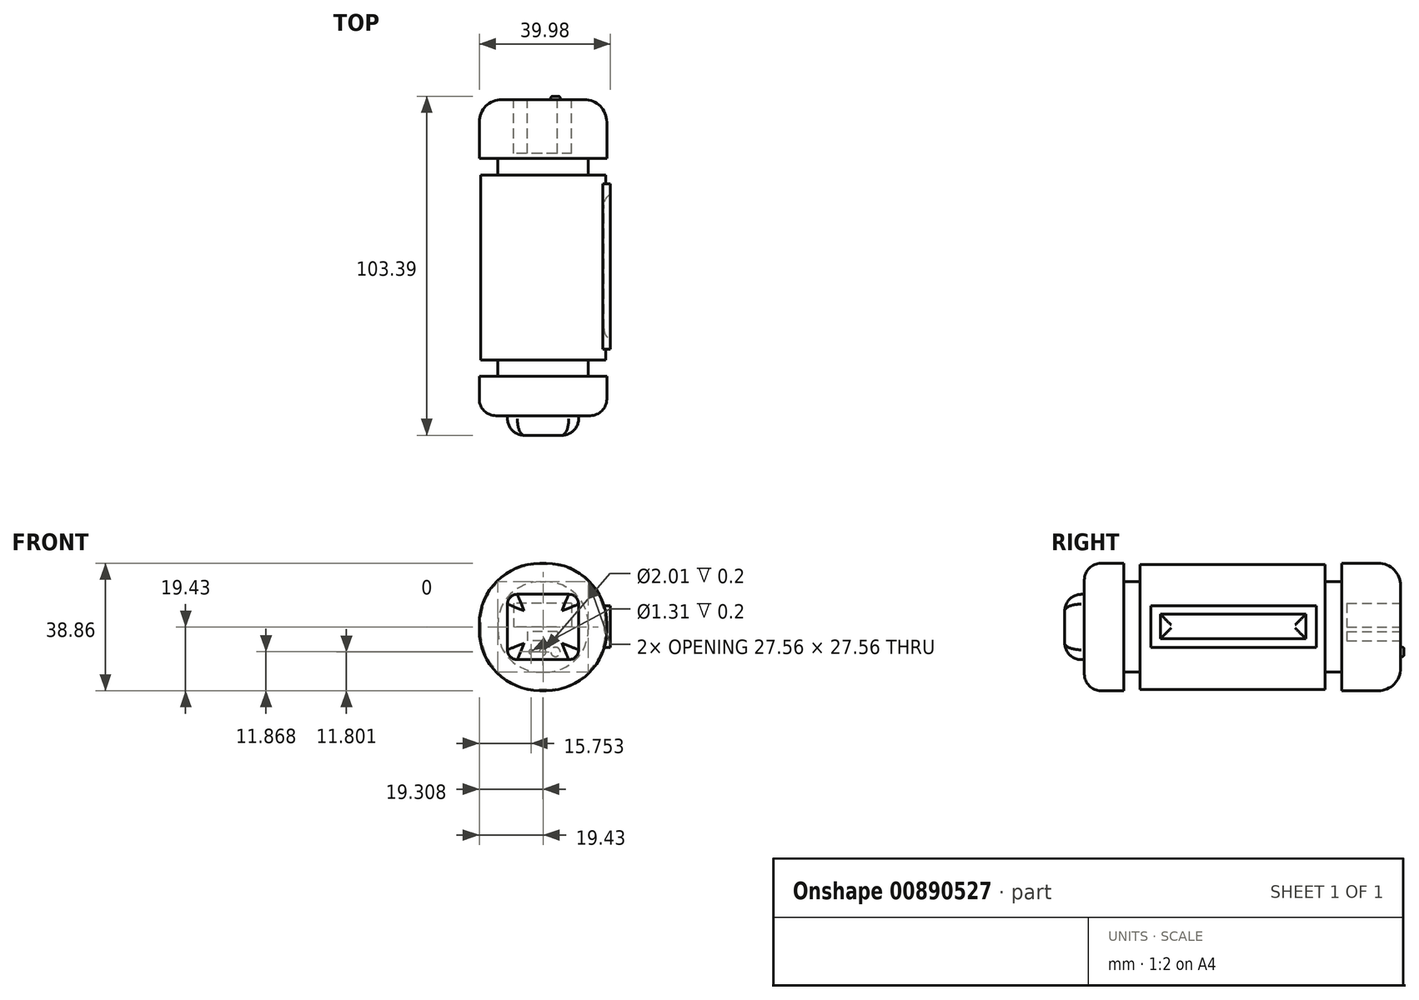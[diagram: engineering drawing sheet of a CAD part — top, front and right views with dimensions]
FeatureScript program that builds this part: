
annotation { "Feature Type Name" : "Feature", "Feature Type Description" : "" }
export const myFeature = defineFeature(function(context is Context, id is Id, definition is map)
    precondition{}
    {
        {
            var Q0;
            Q0=qCreatedBy(makeId("Front.planeOp"),FACE);
            var sketch = newSketch(context, id + "F0", { "sketchPlane" : qUnion([Q0])});
            skLineSegment(sketch, "E0.bottom", {"start": v(19.05, 19.05) * mm, "end": v(-19.05, 19.05) * mm});
            skLineSegment(sketch, "E0.top", {"start": v(19.05, -19.05) * mm, "end": v(-19.05, -19.05) * mm});
            skLineSegment(sketch, "E0.left", {"start": v(19.05, 19.05) * mm, "end": v(19.05, -19.05) * mm});
            skLineSegment(sketch, "E0.right", {"start": v(-19.05, 19.05) * mm, "end": v(-19.05, -19.05) * mm});
            skPoint(sketch, "E0.middle", {"position": v(0, 0) * mm});
            skSolve(sketch);
        }
        {
            var Q0;
            Q0=makeQuery(id+"F0.imprint","IMPRINT",FACE,{"disambiguationData":[TD([[makeQuery(id+"F0.imprint","IMPRINT",EDGE,{"derivedFrom":sQuery(id+"F0.wireOp",EDGE,"E0.bottom")}),1.0]])]});
            extrude(context, id + "F1", {"entities" : qUnion([Q0]), "depth" : 25.4 * mm, "offsetDistance" : 25.4 * mm});
        }
        {
            var Q0;
            Q0=makeQuery(id+"F1.opExtrude","CAP_FACE",FACE,{"disambiguationData":[OSD([sQuery(id+"F0.wireOp",EDGE,"E0.bottom"),sQuery(id+"F0.wireOp",EDGE,"E0.top"),sQuery(id+"F0.wireOp",EDGE,"E0.left"),sQuery(id+"F0.wireOp",EDGE,"E0.right")])],"isStart":false});
            extrude(context, id + "F2", {"entities" : qUnion([Q0]), "operationType" : NewBodyOperationType.ADD, "depth" : 30.99 * mm, "offsetDistance" : 25.4 * mm});
        }
        {
            var Q0;
            {var subQ0=sQuery(id+"F0.wireOp",EDGE,"E0.left");Q0=makeQuery(id+"F2.boolean.opBoolean","MERGE",FACE,{"derivedFrom":[makeQuery(id+"F1.opExtrude","SWEPT_FACE",FACE,{"disambiguationData":[OSD([subQ0])]}),makeQuery(id+"F2.opExtrude","SWEPT_FACE",FACE,{"disambiguationData":[OSD([subQ0])]})]});}
            var sketch = newSketch(context, id + "F3", { "sketchPlane" : qUnion([Q0])});
            skLineSegment(sketch, "E1.bottom", {"start": v(-53.1, 6.48) * mm, "end": v(-2.73, 6.48) * mm});
            skLineSegment(sketch, "E1.top", {"start": v(-53.1, -6.19) * mm, "end": v(-2.73, -6.19) * mm});
            skLineSegment(sketch, "E1.left", {"start": v(-53.1, 6.48) * mm, "end": v(-53.1, -6.19) * mm});
            skLineSegment(sketch, "E1.right", {"start": v(-2.73, 6.48) * mm, "end": v(-2.73, -6.19) * mm});
            skSolve(sketch);
        }
        {
            var Q0;
            Q0=makeQuery(id+"F3.imprint","IMPRINT",FACE,{"disambiguationData":[TD([[makeQuery(id+"F3.imprint","IMPRINT",EDGE,{"derivedFrom":sQuery(id+"F3.wireOp",EDGE,"E1.bottom")}),-1.0]])]});
            extrude(context, id + "F4", {"entities" : qUnion([Q0]), "operationType" : NewBodyOperationType.ADD, "depth" : 1.5 * mm, "offsetDistance" : 25.4 * mm});
        }
        {
            var Q0;
            Q0=makeQuery(id+"F4.opExtrude","CAP_FACE",FACE,{"disambiguationData":[OSD([sQuery(id+"F3.wireOp",EDGE,"E1.bottom"),sQuery(id+"F3.wireOp",EDGE,"E1.top"),sQuery(id+"F3.wireOp",EDGE,"E1.left"),sQuery(id+"F3.wireOp",EDGE,"E1.right")])],"isStart":false});
            var sketch = newSketch(context, id + "F5", { "sketchPlane" : qUnion([Q0])});
            skLineSegment(sketch, "E2.bottom", {"start": v(-50.22, 3.89) * mm, "end": v(-5.9, 3.89) * mm});
            skLineSegment(sketch, "E2.top", {"start": v(-50.22, -3.6) * mm, "end": v(-5.9, -3.6) * mm});
            skLineSegment(sketch, "E2.left", {"start": v(-50.22, 3.89) * mm, "end": v(-50.22, -3.6) * mm});
            skLineSegment(sketch, "E2.right", {"start": v(-5.9, 3.89) * mm, "end": v(-5.9, -3.6) * mm});
            skSolve(sketch);
        }
        {
            var Q0;
            Q0=makeQuery(id+"F5.imprint","IMPRINT",FACE,{"disambiguationData":[TD([[makeQuery(id+"F5.imprint","IMPRINT",EDGE,{"derivedFrom":sQuery(id+"F5.wireOp",EDGE,"E2.bottom")}),-1.0]])]});
            extrude(context, id + "F6", {"entities" : qUnion([Q0]), "operationType" : NewBodyOperationType.REMOVE, "oppositeDirection" : true, "depth" : 2 * mm, "offsetDistance" : 25.4 * mm});
        }
        {
            var Q0;
            Q0=makeQuery(id+"F6.boolean.opBoolean","COPY",FACE,{"derivedFrom":makeQuery(id+"F6.opExtrude","CAP_FACE",FACE,{"disambiguationData":[OSD([sQuery(id+"F5.wireOp",EDGE,"E2.bottom"),sQuery(id+"F5.wireOp",EDGE,"E2.top"),sQuery(id+"F5.wireOp",EDGE,"E2.left"),sQuery(id+"F5.wireOp",EDGE,"E2.right")])],"isStart":false})});
            fillet(context, id + "F7", {"entities" : qUnion([Q0]), "radius" : 3.68 * mm, "tangentPropagation" : true, "allowEdgeOverflow" : false});
        }
        {
            var Q0;
            {var subQ0=sQuery(id+"F0.wireOp",EDGE,"E0.right");var subQ1=sQuery(id+"F0.wireOp",EDGE,"E0.bottom");Q0=makeQuery(id+"F2.boolean.opBoolean","MERGE",EDGE,{"derivedFrom":[makeQuery(id+"F1.opExtrude","SWEPT_EDGE",EDGE,{"disambiguationData":[OSD([subQ1,subQ0])]}),makeQuery(id+"F2.opExtrude","SWEPT_EDGE",EDGE,{"disambiguationData":[OSD([subQ1,subQ0])]})]});}
            var Q1;
            {var subQ0=sQuery(id+"F0.wireOp",EDGE,"E0.left");var subQ1=sQuery(id+"F0.wireOp",EDGE,"E0.bottom");Q1=makeQuery(id+"F2.boolean.opBoolean","MERGE",EDGE,{"derivedFrom":[makeQuery(id+"F1.opExtrude","SWEPT_EDGE",EDGE,{"disambiguationData":[OSD([subQ1,subQ0])]}),makeQuery(id+"F2.opExtrude","SWEPT_EDGE",EDGE,{"disambiguationData":[OSD([subQ1,subQ0])]})]});}
            var Q2;
            {var subQ0=sQuery(id+"F0.wireOp",EDGE,"E0.left");var subQ1=sQuery(id+"F0.wireOp",EDGE,"E0.top");Q2=makeQuery(id+"F2.boolean.opBoolean","MERGE",EDGE,{"derivedFrom":[makeQuery(id+"F1.opExtrude","SWEPT_EDGE",EDGE,{"disambiguationData":[OSD([subQ1,subQ0])]}),makeQuery(id+"F2.opExtrude","SWEPT_EDGE",EDGE,{"disambiguationData":[OSD([subQ1,subQ0])]})]});}
            var Q3;
            {var subQ0=sQuery(id+"F0.wireOp",EDGE,"E0.right");var subQ1=sQuery(id+"F0.wireOp",EDGE,"E0.top");Q3=makeQuery(id+"F2.boolean.opBoolean","MERGE",EDGE,{"derivedFrom":[makeQuery(id+"F1.opExtrude","SWEPT_EDGE",EDGE,{"disambiguationData":[OSD([subQ1,subQ0])]}),makeQuery(id+"F2.opExtrude","SWEPT_EDGE",EDGE,{"disambiguationData":[OSD([subQ1,subQ0])]})]});}
            fillet(context, id + "F8", {"entities" : qUnion([Q0, Q1, Q2, Q3]), "radius" : 18 * mm, "tangentPropagation" : true, "allowEdgeOverflow" : false});
        }
        {
            var Q0;
            Q0=makeQuery(id+"F2.opExtrude","CAP_FACE",FACE,{"disambiguationData":[OSD([sQuery(id+"F0.wireOp",EDGE,"E0.bottom"),sQuery(id+"F0.wireOp",EDGE,"E0.top"),sQuery(id+"F0.wireOp",EDGE,"E0.left"),sQuery(id+"F0.wireOp",EDGE,"E0.right")])],"isStart":false});
            var sketch = newSketch(context, id + "F9", { "sketchPlane" : qUnion([Q0])});
            skLineSegment(sketch, "E3.bottom", {"start": v(13.78, 13.78) * mm, "end": v(-13.78, 13.78) * mm});
            skLineSegment(sketch, "E3.top", {"start": v(13.78, -13.78) * mm, "end": v(-13.78, -13.78) * mm});
            skLineSegment(sketch, "E3.left", {"start": v(13.78, 13.78) * mm, "end": v(13.78, -13.78) * mm});
            skLineSegment(sketch, "E3.right", {"start": v(-13.78, 13.78) * mm, "end": v(-13.78, -13.78) * mm});
            skPoint(sketch, "E3.middle", {"position": v(0, 0) * mm});
            skSolve(sketch);
        }
        {
            var Q0;
            Q0=makeQuery(id+"F9.imprint","IMPRINT",FACE,{"disambiguationData":[TD([[makeQuery(id+"F9.imprint","IMPRINT",EDGE,{"derivedFrom":sQuery(id+"F9.wireOp",EDGE,"E3.bottom")}),1.0]])]});
            extrude(context, id + "F10", {"entities" : qUnion([Q0]), "operationType" : NewBodyOperationType.ADD, "depth" : 5 * mm, "offsetDistance" : 25.4 * mm});
        }
        {
            var Q0;
            Q0=makeQuery(id+"F10.opExtrude","SWEPT_EDGE",EDGE,{"disambiguationData":[OSD([sQuery(id+"F0.wireOp",EDGE,"E0.bottom"),sQuery(id+"F0.wireOp",EDGE,"E0.top"),sQuery(id+"F0.wireOp",EDGE,"E0.left"),sQuery(id+"F0.wireOp",EDGE,"E0.right"),sQuery(id+"F9.wireOp",EDGE,"E3.bottom"),sQuery(id+"F9.wireOp",EDGE,"E3.right")])]});
            var Q1;
            Q1=makeQuery(id+"F10.opExtrude","SWEPT_EDGE",EDGE,{"disambiguationData":[OSD([sQuery(id+"F0.wireOp",EDGE,"E0.bottom"),sQuery(id+"F0.wireOp",EDGE,"E0.top"),sQuery(id+"F0.wireOp",EDGE,"E0.left"),sQuery(id+"F0.wireOp",EDGE,"E0.right"),sQuery(id+"F9.wireOp",EDGE,"E3.top"),sQuery(id+"F9.wireOp",EDGE,"E3.right")])]});
            var Q2;
            Q2=makeQuery(id+"F10.opExtrude","SWEPT_EDGE",EDGE,{"disambiguationData":[OSD([sQuery(id+"F0.wireOp",EDGE,"E0.bottom"),sQuery(id+"F0.wireOp",EDGE,"E0.top"),sQuery(id+"F0.wireOp",EDGE,"E0.left"),sQuery(id+"F0.wireOp",EDGE,"E0.right"),sQuery(id+"F9.wireOp",EDGE,"E3.bottom"),sQuery(id+"F9.wireOp",EDGE,"E3.left")])]});
            var Q3;
            Q3=makeQuery(id+"F10.opExtrude","SWEPT_EDGE",EDGE,{"disambiguationData":[OSD([sQuery(id+"F0.wireOp",EDGE,"E0.bottom"),sQuery(id+"F0.wireOp",EDGE,"E0.top"),sQuery(id+"F0.wireOp",EDGE,"E0.left"),sQuery(id+"F0.wireOp",EDGE,"E0.right"),sQuery(id+"F9.wireOp",EDGE,"E3.top"),sQuery(id+"F9.wireOp",EDGE,"E3.left")])]});
            fillet(context, id + "F11", {"entities" : qUnion([Q0, Q1, Q2, Q3]), "radius" : 13 * mm, "tangentPropagation" : true, "allowEdgeOverflow" : false});
        }
        {
            var Q0;
            Q0=makeQuery(id+"F1.opExtrude","CAP_FACE",FACE,{"disambiguationData":[OSD([sQuery(id+"F0.wireOp",EDGE,"E0.bottom"),sQuery(id+"F0.wireOp",EDGE,"E0.top"),sQuery(id+"F0.wireOp",EDGE,"E0.left"),sQuery(id+"F0.wireOp",EDGE,"E0.right")])],"isStart":true});
            var sketch = newSketch(context, id + "F12", { "sketchPlane" : qUnion([Q0])});
            skLineSegment(sketch, "E4.bottom", {"start": v(13.78, 13.78) * mm, "end": v(-13.78, 13.78) * mm});
            skLineSegment(sketch, "E4.top", {"start": v(13.78, -13.78) * mm, "end": v(-13.78, -13.78) * mm});
            skLineSegment(sketch, "E4.left", {"start": v(13.78, 13.78) * mm, "end": v(13.78, -13.78) * mm});
            skLineSegment(sketch, "E4.right", {"start": v(-13.78, 13.78) * mm, "end": v(-13.78, -13.78) * mm});
            skPoint(sketch, "E4.middle", {"position": v(0, 0) * mm});
            skSolve(sketch);
        }
        {
            var Q0;
            Q0=makeQuery(id+"F12.imprint","IMPRINT",FACE,{"disambiguationData":[TD([[makeQuery(id+"F12.imprint","IMPRINT",EDGE,{"derivedFrom":sQuery(id+"F12.wireOp",EDGE,"E4.bottom")}),1.0]])]});
            extrude(context, id + "F13", {"entities" : qUnion([Q0]), "operationType" : NewBodyOperationType.ADD, "depth" : 5 * mm, "offsetDistance" : 25.4 * mm});
        }
        {
            var Q0;
            Q0=makeQuery(id+"F13.opExtrude","SWEPT_EDGE",EDGE,{"disambiguationData":[OSD([sQuery(id+"F0.wireOp",EDGE,"E0.bottom"),sQuery(id+"F0.wireOp",EDGE,"E0.top"),sQuery(id+"F0.wireOp",EDGE,"E0.left"),sQuery(id+"F0.wireOp",EDGE,"E0.right"),sQuery(id+"F12.wireOp",EDGE,"E4.bottom"),sQuery(id+"F12.wireOp",EDGE,"E4.right")])]});
            var Q1;
            Q1=makeQuery(id+"F13.opExtrude","SWEPT_EDGE",EDGE,{"disambiguationData":[OSD([sQuery(id+"F0.wireOp",EDGE,"E0.bottom"),sQuery(id+"F0.wireOp",EDGE,"E0.top"),sQuery(id+"F0.wireOp",EDGE,"E0.left"),sQuery(id+"F0.wireOp",EDGE,"E0.right"),sQuery(id+"F12.wireOp",EDGE,"E4.top"),sQuery(id+"F12.wireOp",EDGE,"E4.right")])]});
            var Q2;
            Q2=makeQuery(id+"F13.opExtrude","SWEPT_EDGE",EDGE,{"disambiguationData":[OSD([sQuery(id+"F0.wireOp",EDGE,"E0.bottom"),sQuery(id+"F0.wireOp",EDGE,"E0.top"),sQuery(id+"F0.wireOp",EDGE,"E0.left"),sQuery(id+"F0.wireOp",EDGE,"E0.right"),sQuery(id+"F12.wireOp",EDGE,"E4.bottom"),sQuery(id+"F12.wireOp",EDGE,"E4.left")])]});
            var Q3;
            Q3=makeQuery(id+"F13.opExtrude","SWEPT_EDGE",EDGE,{"disambiguationData":[OSD([sQuery(id+"F0.wireOp",EDGE,"E0.bottom"),sQuery(id+"F0.wireOp",EDGE,"E0.top"),sQuery(id+"F0.wireOp",EDGE,"E0.left"),sQuery(id+"F0.wireOp",EDGE,"E0.right"),sQuery(id+"F12.wireOp",EDGE,"E4.top"),sQuery(id+"F12.wireOp",EDGE,"E4.left")])]});
            fillet(context, id + "F14", {"entities" : qUnion([Q0, Q1, Q2, Q3]), "radius" : 13 * mm, "tangentPropagation" : true, "allowEdgeOverflow" : false});
        }
        {
            var Q0;
            Q0=makeQuery(id+"F10.opExtrude","CAP_FACE",FACE,{"disambiguationData":[OSD([sQuery(id+"F9.wireOp",EDGE,"E3.bottom"),sQuery(id+"F9.wireOp",EDGE,"E3.top"),sQuery(id+"F9.wireOp",EDGE,"E3.left"),sQuery(id+"F9.wireOp",EDGE,"E3.right")])],"isStart":false});
            var sketch = newSketch(context, id + "F15", { "sketchPlane" : qUnion([Q0])});
            skLineSegment(sketch, "E5.bottom", {"start": v(19.43, 19.43) * mm, "end": v(-19.43, 19.43) * mm});
            skLineSegment(sketch, "E5.top", {"start": v(19.43, -19.43) * mm, "end": v(-19.43, -19.43) * mm});
            skLineSegment(sketch, "E5.left", {"start": v(19.43, 19.43) * mm, "end": v(19.43, -19.43) * mm});
            skLineSegment(sketch, "E5.right", {"start": v(-19.43, 19.43) * mm, "end": v(-19.43, -19.43) * mm});
            skPoint(sketch, "E5.middle", {"position": v(0, 0) * mm});
            skSolve(sketch);
        }
        {
            var Q0;
            Q0=makeQuery(id+"F15.imprint","IMPRINT",FACE,{"disambiguationData":[TD([[makeQuery(id+"F15.imprint","IMPRINT",EDGE,{"derivedFrom":sQuery(id+"F15.wireOp",EDGE,"E5.bottom")}),1.0]])]});
            var Q1;
            {var subQ3=sQuery(id+"F9.wireOp",EDGE,"E3.bottom");Q1=makeQuery(id+"F15.imprint","IMPRINT",FACE,{"disambiguationData":[TD([[makeQuery(id+"F15.imprint","IMPRINT",EDGE,{"derivedFrom":makeQuery(id+"F10.opExtrude","CAP_EDGE",EDGE,{"disambiguationData":[OSD([subQ3])],"isStart":false})}),1.0]])]});}
            extrude(context, id + "F16", {"entities" : qUnion([Q0, Q1]), "operationType" : NewBodyOperationType.ADD, "depth" : 12 * mm, "offsetDistance" : 25.4 * mm});
        }
        {
            var Q0;
            Q0=makeQuery(id+"F16.opExtrude","SWEPT_EDGE",EDGE,{"disambiguationData":[OSD([sQuery(id+"F15.wireOp",EDGE,"E5.bottom"),sQuery(id+"F15.wireOp",EDGE,"E5.right")])]});
            var Q1;
            Q1=makeQuery(id+"F16.opExtrude","SWEPT_EDGE",EDGE,{"disambiguationData":[OSD([sQuery(id+"F15.wireOp",EDGE,"E5.bottom"),sQuery(id+"F15.wireOp",EDGE,"E5.left")])]});
            var Q2;
            Q2=makeQuery(id+"F16.opExtrude","SWEPT_EDGE",EDGE,{"disambiguationData":[OSD([sQuery(id+"F15.wireOp",EDGE,"E5.top"),sQuery(id+"F15.wireOp",EDGE,"E5.right")])]});
            var Q3;
            Q3=makeQuery(id+"F16.opExtrude","SWEPT_EDGE",EDGE,{"disambiguationData":[OSD([sQuery(id+"F15.wireOp",EDGE,"E5.top"),sQuery(id+"F15.wireOp",EDGE,"E5.left")])]});
            fillet(context, id + "F17", {"entities" : qUnion([Q0, Q1, Q2, Q3]), "radius" : 18.5 * mm, "tangentPropagation" : true, "allowEdgeOverflow" : false});
        }
        {
            var Q0;
            Q0=makeQuery(id+"F13.opExtrude","CAP_FACE",FACE,{"disambiguationData":[OSD([sQuery(id+"F12.wireOp",EDGE,"E4.bottom"),sQuery(id+"F12.wireOp",EDGE,"E4.top"),sQuery(id+"F12.wireOp",EDGE,"E4.left"),sQuery(id+"F12.wireOp",EDGE,"E4.right")])],"isStart":false});
            var sketch = newSketch(context, id + "F18", { "sketchPlane" : qUnion([Q0])});
            skLineSegment(sketch, "E6.bottom", {"start": v(20, 20) * mm, "end": v(-20, 20) * mm});
            skLineSegment(sketch, "E6.top", {"start": v(20, -20) * mm, "end": v(-20, -20) * mm});
            skLineSegment(sketch, "E6.left", {"start": v(20, 20) * mm, "end": v(20, -20) * mm});
            skLineSegment(sketch, "E6.right", {"start": v(-20, 20) * mm, "end": v(-20, -20) * mm});
            skPoint(sketch, "E6.middle", {"position": v(0, 0) * mm});
            skLineSegment(sketch, "E7.bottom", {"start": v(19.43, 19.43) * mm, "end": v(-19.43, 19.43) * mm});
            skLineSegment(sketch, "E7.top", {"start": v(19.43, -19.43) * mm, "end": v(-19.43, -19.43) * mm});
            skLineSegment(sketch, "E7.left", {"start": v(19.43, 19.43) * mm, "end": v(19.43, -19.43) * mm});
            skLineSegment(sketch, "E7.right", {"start": v(-19.43, 19.43) * mm, "end": v(-19.43, -19.43) * mm});
            skSolve(sketch);
        }
        {
            var Q0;
            Q0=makeQuery(id+"F18.imprint","IMPRINT",FACE,{"disambiguationData":[TD([[makeQuery(id+"F18.imprint","IMPRINT",EDGE,{"derivedFrom":sQuery(id+"F18.wireOp",EDGE,"E7.bottom")}),1.0]])]});
            var Q1;
            {var subQ3=sQuery(id+"F12.wireOp",EDGE,"E4.bottom");Q1=makeQuery(id+"F18.imprint","IMPRINT",FACE,{"disambiguationData":[TD([[makeQuery(id+"F18.imprint","IMPRINT",EDGE,{"derivedFrom":makeQuery(id+"F13.opExtrude","CAP_EDGE",EDGE,{"disambiguationData":[OSD([subQ3])],"isStart":false})}),1.0]])]});}
            extrude(context, id + "F19", {"entities" : qUnion([Q0, Q1]), "operationType" : NewBodyOperationType.ADD, "depth" : 18 * mm, "offsetDistance" : 25.4 * mm});
        }
        {
            var Q0;
            Q0=makeQuery(id+"F19.opExtrude","SWEPT_EDGE",EDGE,{"disambiguationData":[OSD([sQuery(id+"F18.wireOp",EDGE,"E7.bottom"),sQuery(id+"F18.wireOp",EDGE,"E7.right")])]});
            var Q1;
            Q1=makeQuery(id+"F19.opExtrude","SWEPT_EDGE",EDGE,{"disambiguationData":[OSD([sQuery(id+"F18.wireOp",EDGE,"E7.bottom"),sQuery(id+"F18.wireOp",EDGE,"E7.left")])]});
            var Q2;
            Q2=makeQuery(id+"F19.opExtrude","SWEPT_EDGE",EDGE,{"disambiguationData":[OSD([sQuery(id+"F18.wireOp",EDGE,"E7.top"),sQuery(id+"F18.wireOp",EDGE,"E7.right")])]});
            var Q3;
            Q3=makeQuery(id+"F19.opExtrude","SWEPT_EDGE",EDGE,{"disambiguationData":[OSD([sQuery(id+"F18.wireOp",EDGE,"E7.top"),sQuery(id+"F18.wireOp",EDGE,"E7.left")])]});
            fillet(context, id + "F20", {"entities" : qUnion([Q0, Q1, Q2, Q3]), "radius" : 18.5 * mm, "tangentPropagation" : true, "allowEdgeOverflow" : false});
        }
        {
            var Q0;
            Q0=makeQuery(id+"F19.opExtrude","CAP_FACE",FACE,{"disambiguationData":[OSD([sQuery(id+"F18.wireOp",EDGE,"E7.bottom"),sQuery(id+"F18.wireOp",EDGE,"E7.top"),sQuery(id+"F18.wireOp",EDGE,"E7.left"),sQuery(id+"F18.wireOp",EDGE,"E7.right")])],"isStart":false});
            fillet(context, id + "F21", {"entities" : qUnion([Q0]), "radius" : 6.86 * mm, "tangentPropagation" : true, "allowEdgeOverflow" : false});
        }
        {
            var Q0;
            Q0=makeQuery(id+"F16.opExtrude","CAP_FACE",FACE,{"disambiguationData":[OSD([sQuery(id+"F15.wireOp",EDGE,"E5.bottom"),sQuery(id+"F15.wireOp",EDGE,"E5.top"),sQuery(id+"F15.wireOp",EDGE,"E5.left"),sQuery(id+"F15.wireOp",EDGE,"E5.right")])],"isStart":false});
            fillet(context, id + "F22", {"entities" : qUnion([Q0]), "radius" : 5.08 * mm, "tangentPropagation" : true, "allowEdgeOverflow" : false});
        }
        {
            var Q0;
            Q0=makeQuery(id+"F16.opExtrude","CAP_FACE",FACE,{"disambiguationData":[OSD([sQuery(id+"F15.wireOp",EDGE,"E5.bottom"),sQuery(id+"F15.wireOp",EDGE,"E5.top"),sQuery(id+"F15.wireOp",EDGE,"E5.left"),sQuery(id+"F15.wireOp",EDGE,"E5.right")])],"isStart":false});
            var sketch = newSketch(context, id + "F23", { "sketchPlane" : qUnion([Q0])});
            skLineSegment(sketch, "E8.bottom", {"start": v(10.84, 9.97) * mm, "end": v(-10.84, 9.97) * mm});
            skLineSegment(sketch, "E8.top", {"start": v(10.84, -9.97) * mm, "end": v(-10.84, -9.97) * mm});
            skLineSegment(sketch, "E8.left", {"start": v(10.84, 9.97) * mm, "end": v(10.84, -9.97) * mm});
            skLineSegment(sketch, "E8.right", {"start": v(-10.84, 9.97) * mm, "end": v(-10.84, -9.97) * mm});
            skPoint(sketch, "E8.middle", {"position": v(0, 0) * mm});
            skSolve(sketch);
        }
        {
            var Q0;
            Q0=makeQuery(id+"F23.imprint","IMPRINT",FACE,{"disambiguationData":[TD([[makeQuery(id+"F23.imprint","IMPRINT",EDGE,{"derivedFrom":sQuery(id+"F23.wireOp",EDGE,"E8.bottom")}),1.0]])]});
            extrude(context, id + "F24", {"entities" : qUnion([Q0]), "operationType" : NewBodyOperationType.ADD, "depth" : 6 * mm, "offsetDistance" : 25.4 * mm});
        }
        {
            var Q0;
            Q0=makeQuery(id+"F24.opExtrude","SWEPT_EDGE",EDGE,{"disambiguationData":[OSD([sQuery(id+"F15.wireOp",EDGE,"E5.bottom"),sQuery(id+"F15.wireOp",EDGE,"E5.top"),sQuery(id+"F15.wireOp",EDGE,"E5.left"),sQuery(id+"F15.wireOp",EDGE,"E5.right"),sQuery(id+"F23.wireOp",EDGE,"E8.bottom"),sQuery(id+"F23.wireOp",EDGE,"E8.right")])]});
            var Q1;
            Q1=makeQuery(id+"F24.opExtrude","SWEPT_EDGE",EDGE,{"disambiguationData":[OSD([sQuery(id+"F15.wireOp",EDGE,"E5.bottom"),sQuery(id+"F15.wireOp",EDGE,"E5.top"),sQuery(id+"F15.wireOp",EDGE,"E5.left"),sQuery(id+"F15.wireOp",EDGE,"E5.right"),sQuery(id+"F23.wireOp",EDGE,"E8.top"),sQuery(id+"F23.wireOp",EDGE,"E8.right")])]});
            var Q2;
            Q2=makeQuery(id+"F24.opExtrude","SWEPT_EDGE",EDGE,{"disambiguationData":[OSD([sQuery(id+"F15.wireOp",EDGE,"E5.bottom"),sQuery(id+"F15.wireOp",EDGE,"E5.top"),sQuery(id+"F15.wireOp",EDGE,"E5.left"),sQuery(id+"F15.wireOp",EDGE,"E5.right"),sQuery(id+"F23.wireOp",EDGE,"E8.bottom"),sQuery(id+"F23.wireOp",EDGE,"E8.left")])]});
            var Q3;
            Q3=makeQuery(id+"F24.opExtrude","SWEPT_EDGE",EDGE,{"disambiguationData":[OSD([sQuery(id+"F15.wireOp",EDGE,"E5.bottom"),sQuery(id+"F15.wireOp",EDGE,"E5.top"),sQuery(id+"F15.wireOp",EDGE,"E5.left"),sQuery(id+"F15.wireOp",EDGE,"E5.right"),sQuery(id+"F23.wireOp",EDGE,"E8.top"),sQuery(id+"F23.wireOp",EDGE,"E8.left")])]});
            fillet(context, id + "F25", {"entities" : qUnion([Q0, Q1, Q2, Q3]), "radius" : 3 * mm, "tangentPropagation" : true, "allowEdgeOverflow" : false});
        }
        {
            var Q0;
            Q0=makeQuery(id+"F24.opExtrude","CAP_FACE",FACE,{"disambiguationData":[OSD([sQuery(id+"F23.wireOp",EDGE,"E8.bottom"),sQuery(id+"F23.wireOp",EDGE,"E8.top"),sQuery(id+"F23.wireOp",EDGE,"E8.left"),sQuery(id+"F23.wireOp",EDGE,"E8.right")])],"isStart":false});
            fillet(context, id + "F26", {"entities" : qUnion([Q0]), "radius" : 5.08 * mm, "tangentPropagation" : true, "allowEdgeOverflow" : false});
        }
        {
            var Q0;
            Q0=makeQuery(id+"F19.opExtrude","CAP_FACE",FACE,{"disambiguationData":[OSD([sQuery(id+"F18.wireOp",EDGE,"E7.bottom"),sQuery(id+"F18.wireOp",EDGE,"E7.top"),sQuery(id+"F18.wireOp",EDGE,"E7.left"),sQuery(id+"F18.wireOp",EDGE,"E7.right")])],"isStart":false});
            var sketch = newSketch(context, id + "F27", { "sketchPlane" : qUnion([Q0])});
            skLineSegment(sketch, "E9.bottom", {"start": v(-8.7, 7.28) * mm, "end": v(9, 7.28) * mm});
            skLineSegment(sketch, "E9.top", {"start": v(-8.7, 0) * mm, "end": v(9, 0) * mm});
            skLineSegment(sketch, "E9.left", {"start": v(-8.7, 7.28) * mm, "end": v(-8.7, 0) * mm});
            skLineSegment(sketch, "E9.right", {"start": v(9, 7.28) * mm, "end": v(9, 0) * mm});
            skSolve(sketch);
        }
        {
            var Q0;
            Q0=makeQuery(id+"F27.imprint","IMPRINT",FACE,{"disambiguationData":[TD([[makeQuery(id+"F27.imprint","IMPRINT",EDGE,{"derivedFrom":sQuery(id+"F27.wireOp",EDGE,"E9.bottom")}),-1.0]])]});
            extrude(context, id + "F28", {"entities" : qUnion([Q0]), "operationType" : NewBodyOperationType.REMOVE, "oppositeDirection" : true, "depth" : 16.4 * mm, "offsetDistance" : 25.4 * mm});
        }
        {
            var Q0;
            Q0=makeQuery(id+"F19.opExtrude","CAP_FACE",FACE,{"disambiguationData":[OSD([sQuery(id+"F18.wireOp",EDGE,"E7.bottom"),sQuery(id+"F18.wireOp",EDGE,"E7.top"),sQuery(id+"F18.wireOp",EDGE,"E7.left"),sQuery(id+"F18.wireOp",EDGE,"E7.right")])],"isStart":false});
            var sketch = newSketch(context, id + "F29", { "sketchPlane" : qUnion([Q0])});
            skLineSegment(sketch, "E10.bottom", {"start": v(-4.42, -1.44) * mm, "end": v(4.78, -1.44) * mm});
            skLineSegment(sketch, "E10.top", {"start": v(-4.42, -4.17) * mm, "end": v(4.78, -4.17) * mm});
            skLineSegment(sketch, "E10.left", {"start": v(-4.42, -1.44) * mm, "end": v(-4.42, -4.17) * mm});
            skLineSegment(sketch, "E10.right", {"start": v(4.78, -1.44) * mm, "end": v(4.78, -4.17) * mm});
            skSolve(sketch);
        }
        {
            var Q0;
            Q0=makeQuery(id+"F29.imprint","IMPRINT",FACE,{"disambiguationData":[TD([[makeQuery(id+"F29.imprint","IMPRINT",EDGE,{"derivedFrom":sQuery(id+"F29.wireOp",EDGE,"E10.bottom")}),-1.0]])]});
            extrude(context, id + "F30", {"entities" : qUnion([Q0]), "operationType" : NewBodyOperationType.REMOVE, "oppositeDirection" : true, "depth" : 16.4 * mm, "offsetDistance" : 25.4 * mm});
        }
        {
            var Q0;
            Q0=makeQuery(id+"F19.opExtrude","CAP_FACE",FACE,{"disambiguationData":[OSD([sQuery(id+"F18.wireOp",EDGE,"E7.bottom"),sQuery(id+"F18.wireOp",EDGE,"E7.top"),sQuery(id+"F18.wireOp",EDGE,"E7.left"),sQuery(id+"F18.wireOp",EDGE,"E7.right")])],"isStart":false});
            var sketch = newSketch(context, id + "F31", { "sketchPlane" : qUnion([Q0])});
            skCircle(sketch, "E11", {"center": v(-3.8, -7.58) * mm, "radius": 1.42 * mm});
            skPoint(sketch, "E11.first.point", {"position": v(-5.18, -7.28) * mm});
            skPoint(sketch, "E11.second.point", {"position": v(-2.87, -8.65) * mm});
            skPoint(sketch, "E11.third.point", {"position": v(-3.9, -9) * mm});
            skSolve(sketch);
        }
        {
            var Q0;
            Q0=makeQuery(id+"F31.imprint","IMPRINT",FACE,{"disambiguationData":[TD([[makeQuery(id+"F31.imprint","IMPRINT",EDGE,{"derivedFrom":sQuery(id+"F31.wireOp",EDGE,"E11")}),1.0]])]});
            extrude(context, id + "F32", {"entities" : qUnion([Q0]), "operationType" : NewBodyOperationType.ADD, "depth" : 1 * mm, "offsetDistance" : 25.4 * mm});
        }
        {
            var Q0;
            Q0=makeQuery(id+"F32.opExtrude","CAP_FACE",FACE,{"disambiguationData":[OSD([sQuery(id+"F31.wireOp",EDGE,"E11")])],"isStart":false});
            var Q1;
            {var subQ0=sQuery(id+"F18.wireOp",EDGE,"E7.right");var subQ1=sQuery(id+"F18.wireOp",EDGE,"E7.left");var subQ2=sQuery(id+"F18.wireOp",EDGE,"E7.top");var subQ3=sQuery(id+"F18.wireOp",EDGE,"E7.bottom");Q1=makeQuery(id+"F21.opFillet","BLEND_FACE",FACE,{"disambiguationData":[OSD([subQ3,subQ2,subQ1,subQ0]),TDD([makeQuery(id+"F20.opFillet","BLEND_EDGE",EDGE,{"blendedFrom":[makeQuery(id+"F19.opExtrude","SWEPT_EDGE",EDGE,{"disambiguationData":[OSD([subQ3,subQ0])]}),makeQuery(id+"F19.opExtrude","CAP_FACE",FACE,{"disambiguationData":[OSD([subQ3,subQ2,subQ1,subQ0])],"isStart":false})],"blendedInto":[makeQuery(id+"F19.opExtrude","CAP_FACE",FACE,{"disambiguationData":[OSD([subQ3,subQ2,subQ1,subQ0])],"isStart":false})]})])]});}
            fillet(context, id + "F33", {"entities" : qUnion([Q0, Q1]), "radius" : 0.5 * mm, "tangentPropagation" : true, "allowEdgeOverflow" : false});
        }
        {
            var Q0;
            Q0=makeQuery(id+"F19.opExtrude","CAP_FACE",FACE,{"disambiguationData":[OSD([sQuery(id+"F18.wireOp",EDGE,"E7.bottom"),sQuery(id+"F18.wireOp",EDGE,"E7.top"),sQuery(id+"F18.wireOp",EDGE,"E7.left"),sQuery(id+"F18.wireOp",EDGE,"E7.right")])],"isStart":false});
            var sketch = newSketch(context, id + "F34", { "sketchPlane" : qUnion([Q0])});
            skCircle(sketch, "E12", {"center": v(0.12, -7.63) * mm, "radius": 1 * mm});
            skPoint(sketch, "E12.first.point", {"position": v(-0.67, -7) * mm});
            skPoint(sketch, "E12.second.point", {"position": v(1, -8.12) * mm});
            skPoint(sketch, "E12.third.point", {"position": v(-0.37, -8.5) * mm});
            skSolve(sketch);
        }
        {
            var Q0;
            Q0=makeQuery(id+"F34.imprint","IMPRINT",FACE,{"disambiguationData":[TD([[makeQuery(id+"F34.imprint","IMPRINT",EDGE,{"derivedFrom":sQuery(id+"F34.wireOp",EDGE,"E12")}),1.0]])]});
            extrude(context, id + "F35", {"entities" : qUnion([Q0]), "operationType" : NewBodyOperationType.REMOVE, "oppositeDirection" : true, "depth" : 0.2 * mm, "offsetDistance" : 25.4 * mm});
        }
        {
            var Q0;
            Q0=makeQuery(id+"F19.opExtrude","CAP_FACE",FACE,{"disambiguationData":[OSD([sQuery(id+"F18.wireOp",EDGE,"E7.bottom"),sQuery(id+"F18.wireOp",EDGE,"E7.top"),sQuery(id+"F18.wireOp",EDGE,"E7.left"),sQuery(id+"F18.wireOp",EDGE,"E7.right")])],"isStart":false});
            var sketch = newSketch(context, id + "F36", { "sketchPlane" : qUnion([Q0])});
            skCircle(sketch, "E13", {"center": v(3.68, -7.56) * mm, "radius": 0.66 * mm});
            skPoint(sketch, "E13.first.point", {"position": v(3.13, -7.2) * mm});
            skPoint(sketch, "E13.second.point", {"position": v(4.3, -7.75) * mm});
            skPoint(sketch, "E13.third.point", {"position": v(3.6, -8.21) * mm});
            skSolve(sketch);
        }
        {
            var Q0;
            Q0=makeQuery(id+"F36.imprint","IMPRINT",FACE,{"disambiguationData":[TD([[makeQuery(id+"F36.imprint","IMPRINT",EDGE,{"derivedFrom":sQuery(id+"F36.wireOp",EDGE,"E13")}),1.0]])]});
            extrude(context, id + "F37", {"entities" : qUnion([Q0]), "operationType" : NewBodyOperationType.REMOVE, "oppositeDirection" : true, "depth" : 0.2 * mm, "offsetDistance" : 25.4 * mm});
        }
    });
